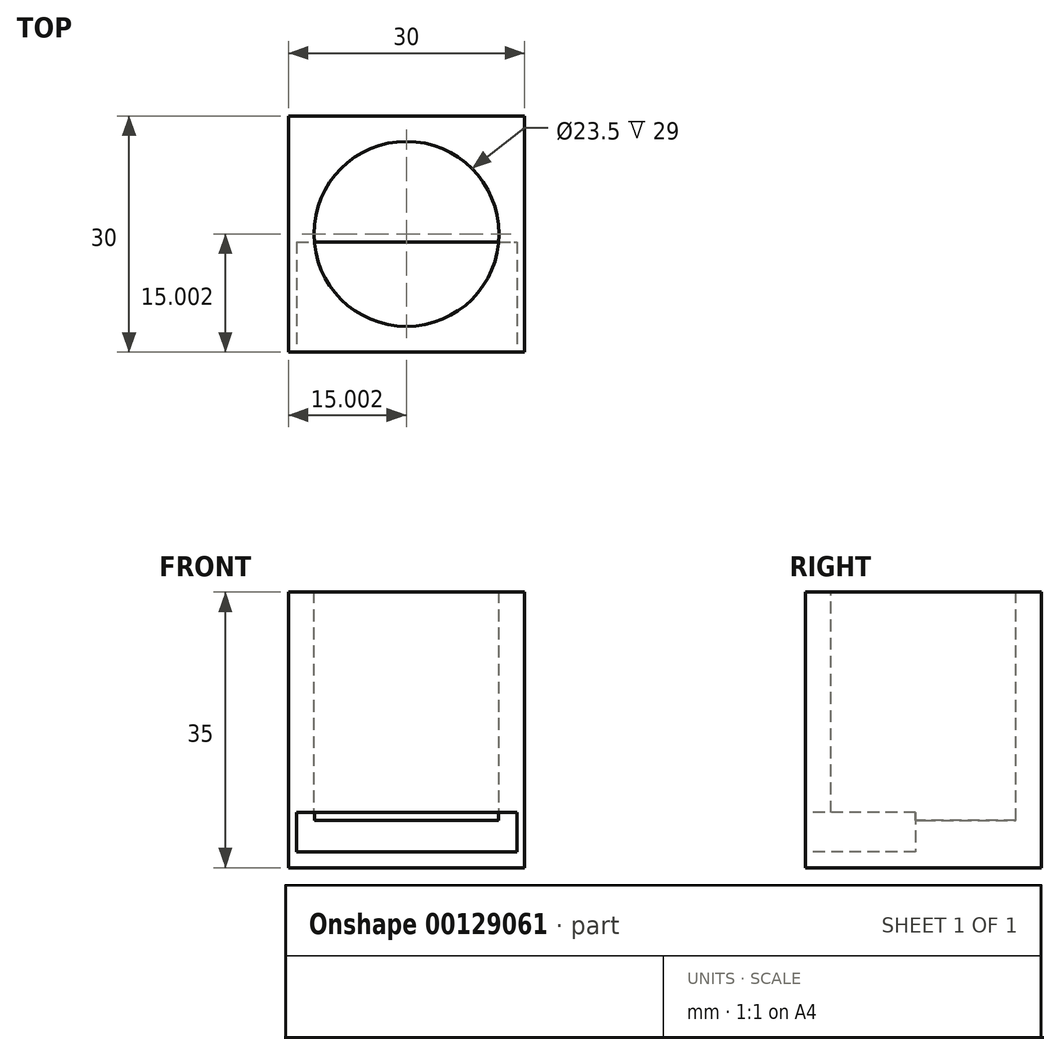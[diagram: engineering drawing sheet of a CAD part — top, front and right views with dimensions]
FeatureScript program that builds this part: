
annotation { "Feature Type Name" : "Feature", "Feature Type Description" : "" }
export const myFeature = defineFeature(function(context is Context, id is Id, definition is map)
    precondition{}
    {
        {
            var Q0;
            Q0=qCreatedBy(makeId("Top.planeOp"),FACE);
            var sketch = newSketch(context, id + "F0", { "sketchPlane" : qUnion([Q0])});
            skLineSegment(sketch, "E0.bottom", {"start": v(-1.06, -57.73) * mm, "end": v(28.94, -57.73) * mm});
            skLineSegment(sketch, "E0.top", {"start": v(-1.06, -87.73) * mm, "end": v(28.94, -87.73) * mm});
            skLineSegment(sketch, "E0.left", {"start": v(-1.06, -57.73) * mm, "end": v(-1.06, -87.73) * mm});
            skLineSegment(sketch, "E0.right", {"start": v(28.94, -57.73) * mm, "end": v(28.94, -87.73) * mm});
            skSolve(sketch);
        }
        {
            var Q0;
            Q0 = qSketchRegion(id + "F0", true);
            extrude(context, id + "F1", {"entities" : qUnion([Q0]), "depth" : 35 * mm});
        }
        {
            var Q0;
            Q0=makeQuery(id+"F1.opExtrude","CAP_FACE",FACE,{"disambiguationData":[OSD([sQuery(id+"F0.wireOp",EDGE,"E0.bottom"),sQuery(id+"F0.wireOp",EDGE,"E0.top"),sQuery(id+"F0.wireOp",EDGE,"E0.left"),sQuery(id+"F0.wireOp",EDGE,"E0.right")])],"isStart":false});
            var sketch = newSketch(context, id + "F2", { "sketchPlane" : qUnion([Q0])});
            skCircle(sketch, "E1", {"center": v(13.94, -72.73) * mm, "radius": 11.75 * mm});
            skPoint(sketch, "E1.centerSnap0", {"position": v(-1.06, -72.73) * mm});
            skSolve(sketch);
        }
        {
            var Q0;
            Q0 = qSketchRegion(id + "F2", true);
            extrude(context, id + "F3", {"entities" : qUnion([Q0]), "operationType" : NewBodyOperationType.REMOVE, "oppositeDirection" : true, "depth" : 29 * mm});
        }
        {
            var Q0;
            Q0=makeQuery(id+"F1.opExtrude","SWEPT_FACE",FACE,{"disambiguationData":[OSD([sQuery(id+"F0.wireOp",EDGE,"E0.top")])]});
            var sketch = newSketch(context, id + "F4", { "sketchPlane" : qUnion([Q0])});
            skLineSegment(sketch, "E2.bottom", {"start": v(0, 7) * mm, "end": v(28, 7) * mm});
            skLineSegment(sketch, "E2.top", {"start": v(0, 2) * mm, "end": v(28, 2) * mm});
            skLineSegment(sketch, "E2.left", {"start": v(0, 7) * mm, "end": v(0, 2) * mm});
            skLineSegment(sketch, "E2.right", {"start": v(28, 7) * mm, "end": v(28, 2) * mm});
            skSolve(sketch);
        }
        {
            var Q0;
            Q0 = qSketchRegion(id + "F4", true);
            extrude(context, id + "F5", {"entities" : qUnion([Q0]), "operationType" : NewBodyOperationType.REMOVE, "oppositeDirection" : true, "depth" : 14 * mm});
        }
    });
